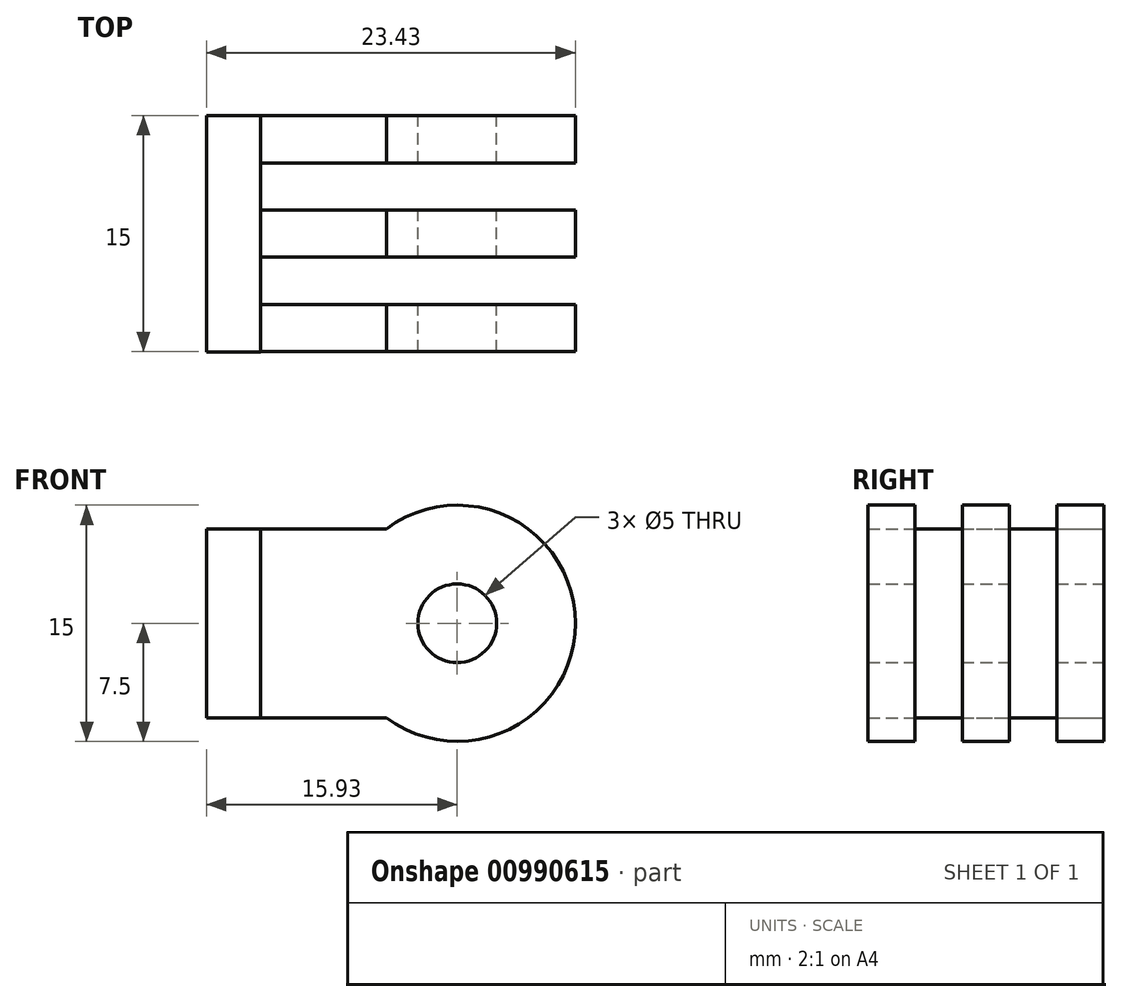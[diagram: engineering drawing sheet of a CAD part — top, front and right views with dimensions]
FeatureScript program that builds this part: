
annotation { "Feature Type Name" : "Feature", "Feature Type Description" : "" }
export const myFeature = defineFeature(function(context is Context, id is Id, definition is map)
    precondition{}
    {
        {
            var Q0;
            Q0=qCreatedBy(makeId("Front.planeOp"),FACE);
            var sketch = newSketch(context, id + "F0", { "sketchPlane" : qUnion([Q0])});
            skCircle(sketch, "E0", {"center": v(0, 0) * mm, "radius": 7.5 * mm});
            skCircle(sketch, "E1", {"center": v(0, 0) * mm, "radius": 2.5 * mm});
            skLineSegment(sketch, "E2.bottom", {"start": v(-4.5, -6) * mm, "end": v(4.5, -6) * mm});
            skLineSegment(sketch, "E2.left", {"start": v(-4.5, -6) * mm, "end": v(-4.5, 6) * mm});
            skLineSegment(sketch, "E2.right", {"start": v(4.5, -6) * mm, "end": v(4.5, 6) * mm});
            skLineSegment(sketch, "E3", {"start": v(-4.5, -6) * mm, "end": v(-12.5, -6) * mm});
            skLineSegment(sketch, "E4", {"start": v(-12.5, -6) * mm, "end": v(-12.5, 6) * mm});
            skLineSegment(sketch, "E5", {"start": v(4.5, 6) * mm, "end": v(-12.5, 6) * mm});
            skSolve(sketch);
        }
        {
            var Q0;
            Q0 = qSketchRegion(id + "F0", true);
            extrude(context, id + "F1", {"entities" : qUnion([Q0]), "endBound" : BoundingType.SYMMETRIC, "depth" : 3 * mm, "offsetDistance" : 25.4 * mm});
        }
        {
            var Q0;
            Q0 = qSketchRegion(id + "F0", true);
            extrude(context, id + "F2", {"entities" : qUnion([Q0]), "oppositeDirection" : true, "depth" : 3 * mm, "offsetDistance" : 25.4 * mm});
        }
        {
            var Q0;
            Q0=makeQuery(id+"F2.opExtrude","SWEPT_BODY",BODY,{"disambiguationData":[OSD([sQuery(id+"F0.wireOp",EDGE,"E0"),sQuery(id+"F0.wireOp",EDGE,"E1"),sQuery(id+"F0.wireOp",EDGE,"E3"),sQuery(id+"F0.wireOp",EDGE,"E4"),sQuery(id+"F0.wireOp",EDGE,"E5")])]});
            transform(context, id + "F3", {"entities" : qUnion([Q0]), "transformType" : TransformType.TRANSLATION_3D, "dx" : 0 * mm, "dy" : 1.5 * mm, "dz" : 0 * mm, "makeCopy" : false});
        }
        {
            var Q0;
            Q0 = qSketchRegion(id + "F0", true);
            extrude(context, id + "F4", {"entities" : qUnion([Q0]), "depth" : 3 * mm, "offsetDistance" : 25.4 * mm});
        }
        {
            var Q0;
            Q0=makeQuery(id+"F4.opExtrude","SWEPT_BODY",BODY,{"disambiguationData":[OSD([sQuery(id+"F0.wireOp",EDGE,"E0"),sQuery(id+"F0.wireOp",EDGE,"E1"),sQuery(id+"F0.wireOp",EDGE,"E3"),sQuery(id+"F0.wireOp",EDGE,"E4"),sQuery(id+"F0.wireOp",EDGE,"E5")])]});
            transform(context, id + "F5", {"entities" : qUnion([Q0]), "transformType" : TransformType.TRANSLATION_3D, "dx" : 0 * mm, "dy" : -1.5 * mm, "dz" : 0 * mm, "makeCopy" : false});
        }
        {
            var Q0;
            Q0 = qSketchRegion(id + "F0", true);
            extrude(context, id + "F6", {"entities" : qUnion([Q0]), "depth" : 3 * mm, "offsetDistance" : 25.4 * mm});
        }
        {
            var Q0;
            Q0=makeQuery(id+"F6.opExtrude","SWEPT_BODY",BODY,{"disambiguationData":[OSD([sQuery(id+"F0.wireOp",EDGE,"E0"),sQuery(id+"F0.wireOp",EDGE,"E1"),sQuery(id+"F0.wireOp",EDGE,"E3"),sQuery(id+"F0.wireOp",EDGE,"E4"),sQuery(id+"F0.wireOp",EDGE,"E5")])]});
            transform(context, id + "F7", {"entities" : qUnion([Q0]), "transformType" : TransformType.TRANSLATION_3D, "dx" : 0 * mm, "dy" : -4.5 * mm, "dz" : 0 * mm, "makeCopy" : false});
        }
        {
            var Q0;
            Q0 = qSketchRegion(id + "F0", true);
            extrude(context, id + "F8", {"entities" : qUnion([Q0]), "depth" : 3 * mm, "offsetDistance" : 25.4 * mm});
        }
        {
            var Q0;
            Q0=makeQuery(id+"F8.opExtrude","SWEPT_BODY",BODY,{"disambiguationData":[OSD([sQuery(id+"F0.wireOp",EDGE,"E0"),sQuery(id+"F0.wireOp",EDGE,"E1"),sQuery(id+"F0.wireOp",EDGE,"E3"),sQuery(id+"F0.wireOp",EDGE,"E4"),sQuery(id+"F0.wireOp",EDGE,"E5")])]});
            transform(context, id + "F9", {"entities" : qUnion([Q0]), "transformType" : TransformType.TRANSLATION_3D, "dx" : 0 * mm, "dy" : 7.5 * mm, "dz" : 0 * mm, "makeCopy" : false});
        }
        {
            var Q0;
            Q0=qCreatedBy(makeId("Front.planeOp"),FACE);
            var sketch = newSketch(context, id + "F10", { "sketchPlane" : qUnion([Q0])});
            skPoint(sketch, "E6.middle", {"position": v(0, 0) * mm});
            skLineSegment(sketch, "E7", {"start": v(-15.96, -6) * mm, "end": v(-15.96, 6) * mm});
            skLineSegment(sketch, "E8", {"start": v(-12.5, 6) * mm, "end": v(-12.5, -6) * mm});
            skLineSegment(sketch, "E9", {"start": v(-15.96, -6) * mm, "end": v(-12.5, -6) * mm});
            skLineSegment(sketch, "E10", {"start": v(-15.96, 6) * mm, "end": v(-12.5, 6) * mm});
            skSolve(sketch);
        }
        {
            var Q0;
            Q0 = qSketchRegion(id + "F10", true);
            extrude(context, id + "F11", {"entities" : qUnion([Q0]), "endBound" : BoundingType.SYMMETRIC, "depth" : 15 * mm, "offsetDistance" : 25.4 * mm});
        }
        {
            var Q0;
            Q0=makeQuery(id+"F11.opExtrude","SWEPT_BODY",BODY,{"disambiguationData":[OSD([sQuery(id+"F10.wireOp",EDGE,"E7"),sQuery(id+"F10.wireOp",EDGE,"E8"),sQuery(id+"F10.wireOp",EDGE,"E9"),sQuery(id+"F10.wireOp",EDGE,"E10")])]});
            transform(context, id + "F12", {"entities" : qUnion([Q0]), "transformType" : TransformType.TRANSLATION_3D, "dx" : 0.03 * mm, "dy" : 0 * mm, "dz" : 0 * mm, "makeCopy" : false});
        }
        {
            var Q0;
            Q0=makeQuery(id+"F4.opExtrude","SWEPT_BODY",BODY,{"disambiguationData":[OSD([sQuery(id+"F0.wireOp",EDGE,"E0"),sQuery(id+"F0.wireOp",EDGE,"E1"),sQuery(id+"F0.wireOp",EDGE,"E3"),sQuery(id+"F0.wireOp",EDGE,"E4"),sQuery(id+"F0.wireOp",EDGE,"E5")])]});
            deleteBodies(context, id + "F13", {"entities" : qUnion([Q0])});
        }
        {
            var Q0;
            Q0=makeQuery(id+"F2.opExtrude","SWEPT_BODY",BODY,{"disambiguationData":[OSD([sQuery(id+"F0.wireOp",EDGE,"E0"),sQuery(id+"F0.wireOp",EDGE,"E1"),sQuery(id+"F0.wireOp",EDGE,"E3"),sQuery(id+"F0.wireOp",EDGE,"E4"),sQuery(id+"F0.wireOp",EDGE,"E5")])]});
            deleteBodies(context, id + "F14", {"entities" : qUnion([Q0])});
        }
    });
